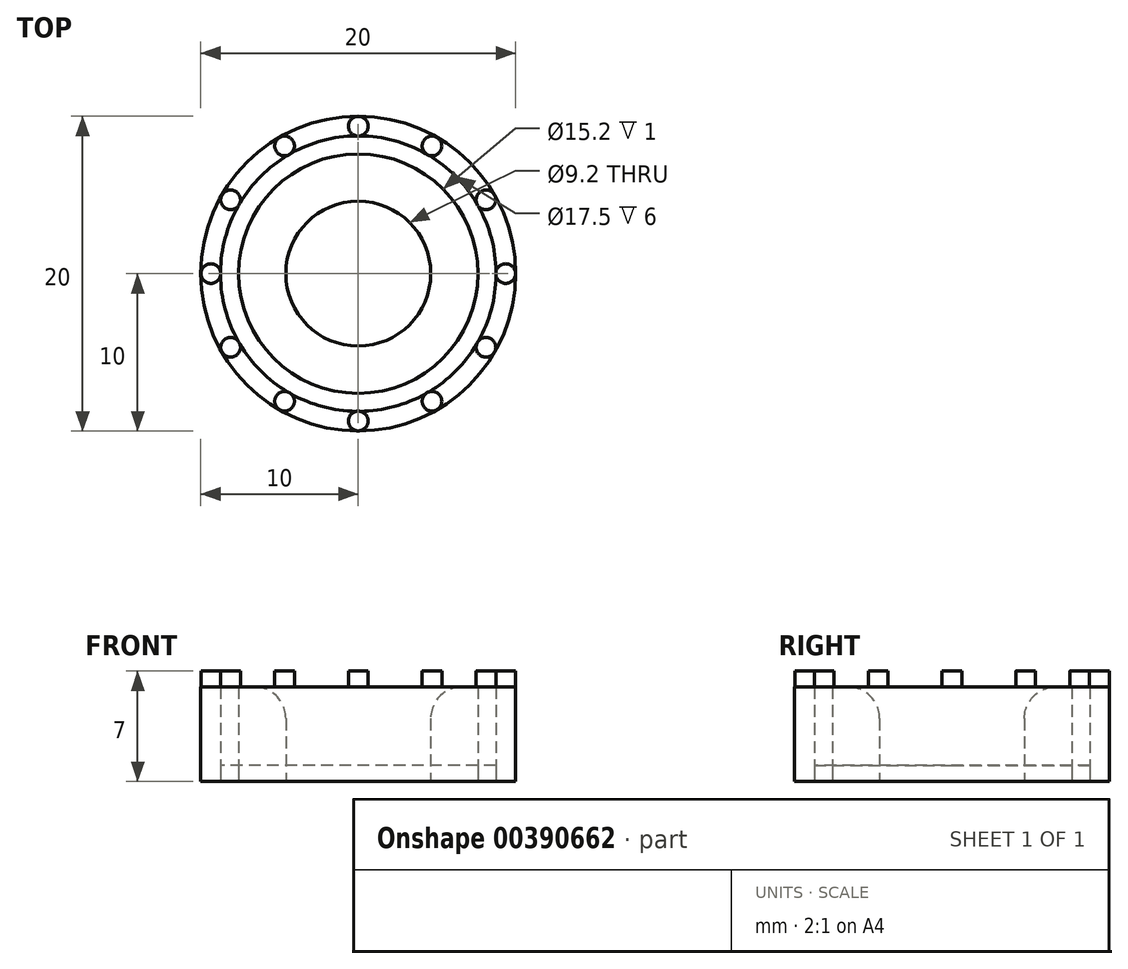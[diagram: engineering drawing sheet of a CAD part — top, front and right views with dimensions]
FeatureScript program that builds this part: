
annotation { "Feature Type Name" : "Feature", "Feature Type Description" : "" }
export const myFeature = defineFeature(function(context is Context, id is Id, definition is map)
    precondition{}
    {
        {
            var Q0;
            Q0=qCreatedBy(makeId("Top.planeOp"),FACE);
            var sketch = newSketch(context, id + "F0", { "sketchPlane" : qUnion([Q0])});
            skCircle(sketch, "E0", {"center": v(0, 0) * mm, "radius": 7.6 * mm});
            skCircle(sketch, "E1", {"center": v(0, 0) * mm, "radius": 4.6 * mm});
            skCircle(sketch, "E2", {"center": v(0, 0) * mm, "radius": 8.75 * mm});
            skCircle(sketch, "E3", {"center": v(0, 0) * mm, "radius": 10 * mm});
            skSolve(sketch);
        }
        {
            var Q0;
            Q0=makeQuery(id+"F0.imprint","IMPRINT",FACE,{"disambiguationData":[TD([[makeQuery(id+"F0.imprint","IMPRINT",EDGE,{"derivedFrom":sQuery(id+"F0.wireOp",EDGE,"E2")}),-1.0]])]});
            var Q1;
            Q1=makeQuery(id+"F0.imprint","IMPRINT",FACE,{"disambiguationData":[TD([[makeQuery(id+"F0.imprint","IMPRINT",EDGE,{"derivedFrom":sQuery(id+"F0.wireOp",EDGE,"E0")}),1.0]])]});
            extrude(context, id + "F1", {"entities" : qUnion([Q0, Q1]), "offsetDistance" : 25 * mm, "depth" : 6 * mm});
        }
        {
            var Q0;
            Q0=makeQuery(id+"F0.imprint","IMPRINT",FACE,{"disambiguationData":[TD([[makeQuery(id+"F0.imprint","IMPRINT",EDGE,{"derivedFrom":sQuery(id+"F0.wireOp",EDGE,"E0")}),-1.0]])]});
            extrude(context, id + "F2", {"entities" : qUnion([Q0]), "offsetDistance" : 25 * mm, "depth" : 1 * mm});
        }
        {
            var Q0;
            Q0=makeQuery(id+"F1.opExtrude","CAP_FACE",FACE,{"disambiguationData":[OSD([sQuery(id+"F0.wireOp",EDGE,"E2"),sQuery(id+"F0.wireOp",EDGE,"E3")])],"isStart":false});
            var sketch = newSketch(context, id + "F3", { "sketchPlane" : qUnion([Q0])});
            skCircle(sketch, "E4", {"center": v(0, 9.36) * mm, "radius": 0.62 * mm});
            skCircle(sketch, "E5.1.0", {"center": v(-4.68, 8.1) * mm, "radius": 0.62 * mm});
            skCircle(sketch, "E5.2.0", {"center": v(-8.1, 4.68) * mm, "radius": 0.62 * mm});
            skCircle(sketch, "E5.3.0", {"center": v(-9.36, 0) * mm, "radius": 0.62 * mm});
            skCircle(sketch, "E5.4.0", {"center": v(-8.1, -4.68) * mm, "radius": 0.62 * mm});
            skCircle(sketch, "E5.5.0", {"center": v(-4.68, -8.1) * mm, "radius": 0.62 * mm});
            skCircle(sketch, "E5.6.0", {"center": v(0, -9.36) * mm, "radius": 0.62 * mm});
            skCircle(sketch, "E5.7.0", {"center": v(4.68, -8.1) * mm, "radius": 0.62 * mm});
            skCircle(sketch, "E5.8.0", {"center": v(8.1, -4.68) * mm, "radius": 0.62 * mm});
            skCircle(sketch, "E5.9.0", {"center": v(9.36, 0) * mm, "radius": 0.62 * mm});
            skCircle(sketch, "E5.10.0", {"center": v(8.1, 4.68) * mm, "radius": 0.62 * mm});
            skCircle(sketch, "E5.11.0", {"center": v(4.68, 8.1) * mm, "radius": 0.62 * mm});
            skPoint(sketch, "E5.center", {"position": v(0, 0) * mm});
            skSolve(sketch);
        }
        {
            var Q0;
            {var subQ0=sQuery(id+"F3.wireOp",EDGE,"E4");var subQ1=makeQuery(id+"F3.imprint","INTERSECT",VERTEX,{"derivedFrom":[makeQuery(id+"F1.opExtrude","CAP_EDGE",EDGE,{"disambiguationData":[OSD([sQuery(id+"F0.wireOp",EDGE,"E3")])],"isStart":false}),subQ0]});Q0=makeQuery(id+"F3.imprint","IMPRINT",FACE,{"disambiguationData":[TD([[makeQuery(id+"F3.imprint","IMPRINT",EDGE,{"disambiguationData":[TD([[subQ1,-1.0]])],"derivedFrom":subQ0}),1.0]])]});}
            extrude(context, id + "F4", {"entities" : qUnion([Q0]), "depth" : 1 * mm, "offsetDistance" : 25 * mm});
        }
        {
            var Q0;
            Q0=makeQuery(id+"F4.opExtrude","SWEPT_BODY",BODY,{"disambiguationData":[OSD([sQuery(id+"F3.wireOp",EDGE,"E4")])]});
            var Q1;
            Q1=makeQuery(id+"F1.opExtrude","CAP_EDGE",EDGE,{"disambiguationData":[OSD([sQuery(id+"F0.wireOp",EDGE,"E2")])],"isStart":false});
            circularPattern(context, id + "F5", {"entities" : qUnion([Q0]), "axis" : qUnion([Q1]), "angle" : 360 * degree, "instanceCount" : 12, "equalSpace" : true});
        }
        {
            var Q0;
            Q0=makeQuery(id+"F1.opExtrude","CAP_EDGE",EDGE,{"disambiguationData":[OSD([sQuery(id+"F0.wireOp",EDGE,"E1")])],"isStart":false});
            fillet(context, id + "F6", {"entities" : qUnion([Q0]), "radius" : 2 * mm, "tangentPropagation" : true, "allowEdgeOverflow" : false});
        }
    });
